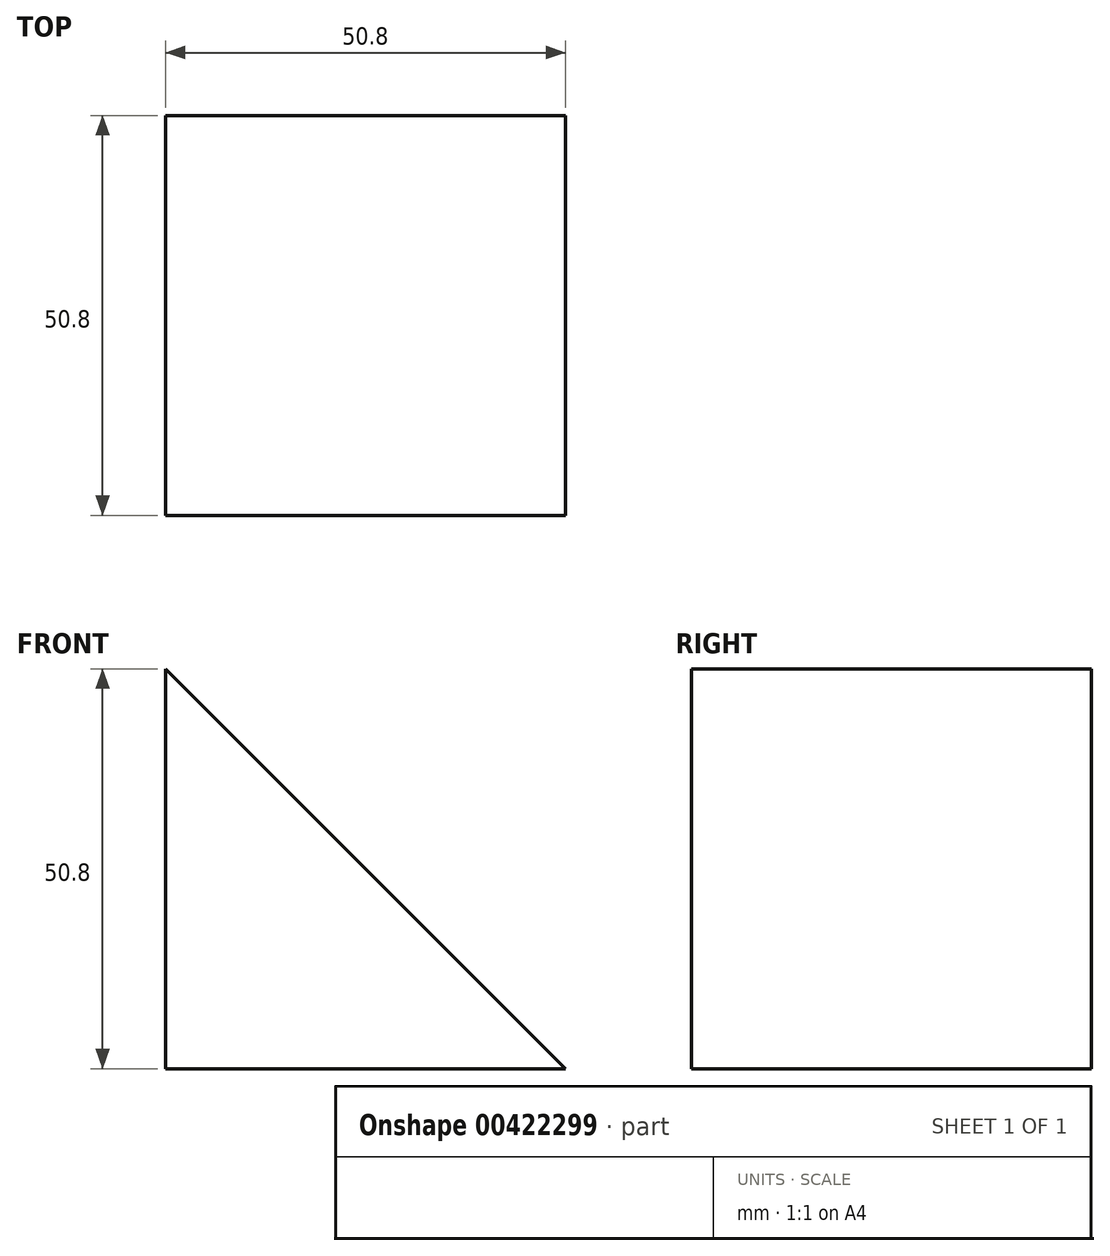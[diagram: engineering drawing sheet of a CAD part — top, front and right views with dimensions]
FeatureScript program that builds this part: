
annotation { "Feature Type Name" : "Feature", "Feature Type Description" : "" }
export const myFeature = defineFeature(function(context is Context, id is Id, definition is map)
    precondition{}
    {
        {
            var Q0;
            Q0=qCreatedBy(makeId("Front.planeOp"),FACE);
            var sketch = newSketch(context, id + "F0", { "sketchPlane" : qUnion([Q0])});
            skLineSegment(sketch, "E0", {"start": v(-59.48, 0) * mm, "end": v(-59.48, 50.8) * mm});
            skLineSegment(sketch, "E1", {"start": v(-59.48, 0) * mm, "end": v(-8.68, 0) * mm});
            skLineSegment(sketch, "E2", {"start": v(-59.48, 50.8) * mm, "end": v(-8.68, 0) * mm});
            skSolve(sketch);
        }
        {
            var Q0;
            Q0 = qSketchRegion(id + "F0", true);
            extrude(context, id + "F1", {"entities" : qUnion([Q0]), "depth" : 50.8 * mm});
        }
    });
